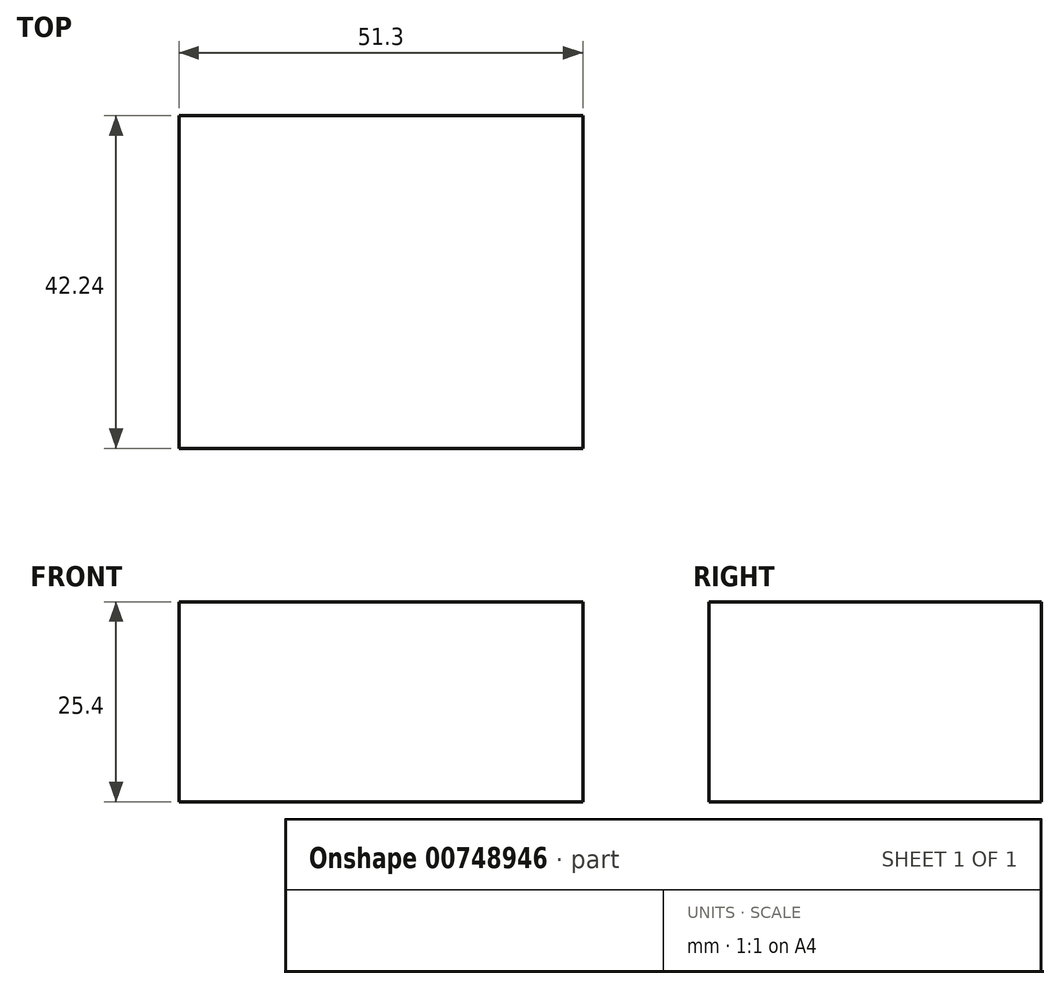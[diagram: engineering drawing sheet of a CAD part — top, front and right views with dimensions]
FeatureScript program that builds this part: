
annotation { "Feature Type Name" : "Feature", "Feature Type Description" : "" }
export const myFeature = defineFeature(function(context is Context, id is Id, definition is map)
    precondition{}
    {
        {
            var Q0;
            Q0=qCreatedBy(makeId("Top.planeOp"),FACE);
            var sketch = newSketch(context, id + "F0", { "sketchPlane" : qUnion([Q0])});
            skLineSegment(sketch, "E0.bottom", {"start": v(-51.3, 0) * mm, "end": v(0, 0) * mm});
            skLineSegment(sketch, "E0.top", {"start": v(-51.3, -42.24) * mm, "end": v(0, -42.24) * mm});
            skLineSegment(sketch, "E0.left", {"start": v(-51.3, 0) * mm, "end": v(-51.3, -42.24) * mm});
            skLineSegment(sketch, "E0.right", {"start": v(0, 0) * mm, "end": v(0, -42.24) * mm});
            skSolve(sketch);
        }
        {
            var Q0;
            Q0=makeQuery(id+"F0.imprint","IMPRINT",FACE,{"disambiguationData":[TD([[makeQuery(id+"F0.imprint","IMPRINT",EDGE,{"derivedFrom":sQuery(id+"F0.wireOp",EDGE,"E0.bottom")}),-1.0]])]});
            extrude(context, id + "F1", {"entities" : qUnion([Q0]), "depth" : 25.4 * mm, "offsetDistance" : 25.4 * mm});
        }
    });
